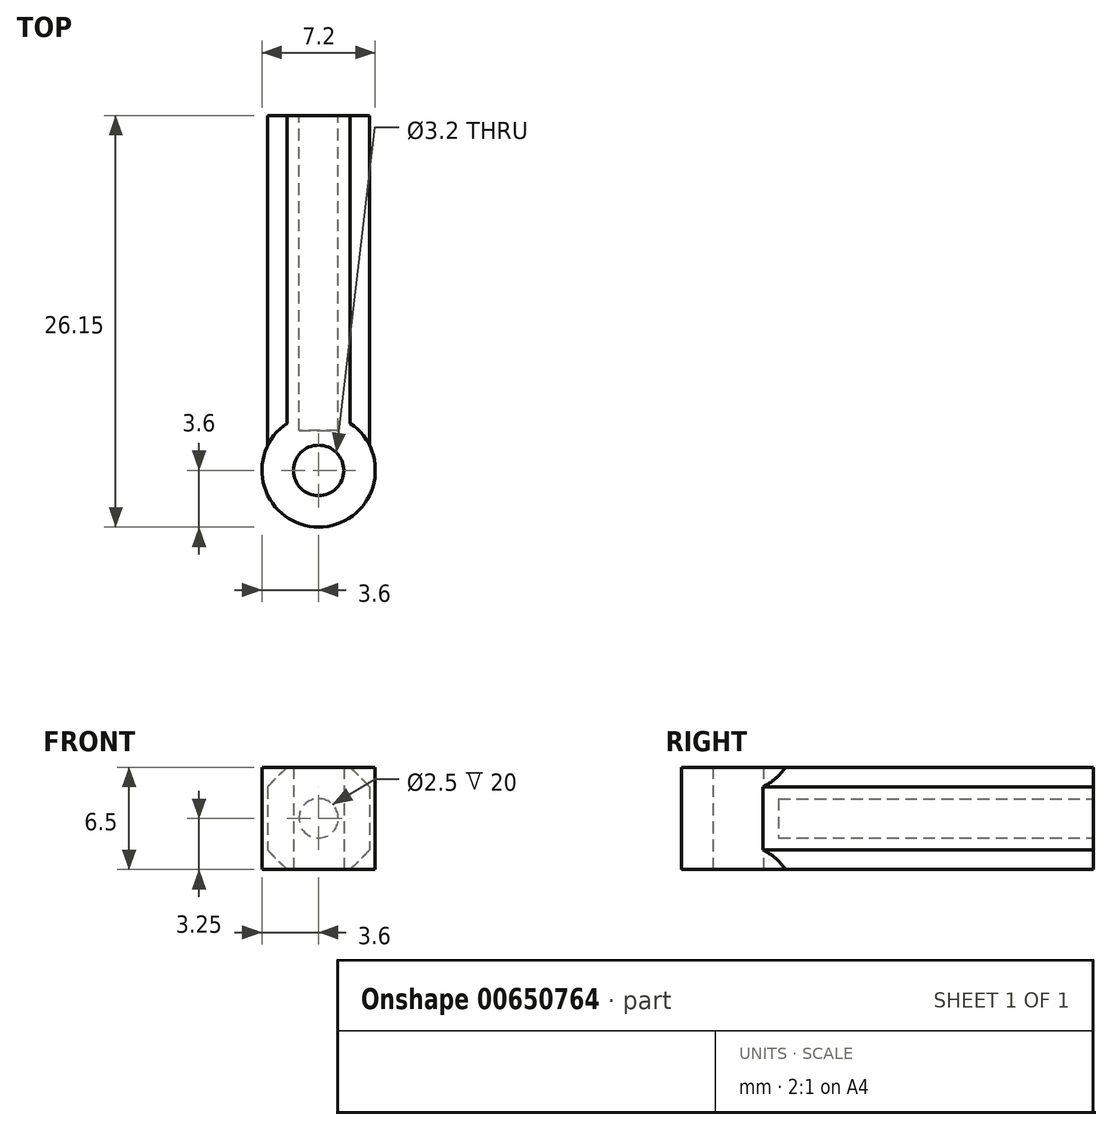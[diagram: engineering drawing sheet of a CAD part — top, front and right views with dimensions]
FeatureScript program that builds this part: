
annotation { "Feature Type Name" : "Feature", "Feature Type Description" : "" }
export const myFeature = defineFeature(function(context is Context, id is Id, definition is map)
    precondition{}
    {
        {
            assignVariable(context, id + "F0", {"name" : "ThreadDiameter", "anyValue" : 2.5});
        }
        {
            assignVariable(context, id + "F1", {"name" : "ThreadLength", "anyValue" : 20});
        }
        {
            var Q0;
            Q0=qCreatedBy(makeId("Top.planeOp"),FACE);
            var sketch = newSketch(context, id + "F2", { "sketchPlane" : qUnion([Q0])});
            skCircle(sketch, "E0", {"center": v(0, 0) * mm, "radius": 1.6 * mm});
            skCircle(sketch, "E1", {"center": v(0, 0) * mm, "radius": 3.6 * mm});
            skLineSegment(sketch, "E2.bottom", {"start": v(-3.25, 1.55) * mm, "end": v(3.25, 1.55) * mm});
            skLineSegment(sketch, "E2.top", {"start": v(-3.25, 22.55) * mm, "end": v(3.25, 22.55) * mm});
            skLineSegment(sketch, "E2.left", {"start": v(-3.25, 1.55) * mm, "end": v(-3.25, 22.55) * mm});
            skLineSegment(sketch, "E2.right", {"start": v(3.25, 1.55) * mm, "end": v(3.25, 22.55) * mm});
            skSolve(sketch);
        }
        {
            var Q0;
            Q0=makeQuery(id+"F2.imprint","IMPRINT",FACE,{"disambiguationData":[TD([[makeQuery(id+"F2.imprint","IMPRINT",EDGE,{"derivedFrom":sQuery(id+"F2.wireOp",EDGE,"E2.top")}),-1.0]])]});
            var Q1;
            {var subQ0=sQuery(id+"F2.wireOp",EDGE,"E2.bottom");var subQ1=sQuery(id+"F2.wireOp",EDGE,"E0");var subQ2=makeQuery(id+"F2.imprint","INTERSECT",VERTEX,{"disambiguationData":[OD(0.0)],"derivedFrom":[subQ1,subQ0]});Q1=makeQuery(id+"F2.imprint","IMPRINT",FACE,{"disambiguationData":[TD([[makeQuery(id+"F2.imprint","IMPRINT",EDGE,{"disambiguationData":[TD([[subQ2,-1.0]])],"derivedFrom":subQ1}),-1.0]])]});}
            var Q2;
            {var subQ0=sQuery(id+"F2.wireOp",EDGE,"E2.bottom");var subQ1=sQuery(id+"F2.wireOp",EDGE,"E0");var subQ2=makeQuery(id+"F2.imprint","INTERSECT",VERTEX,{"disambiguationData":[OD(0.0)],"derivedFrom":[subQ1,subQ0]});Q2=makeQuery(id+"F2.imprint","IMPRINT",FACE,{"disambiguationData":[TD([[makeQuery(id+"F2.imprint","IMPRINT",EDGE,{"disambiguationData":[TD([[subQ2,1.0]])],"derivedFrom":subQ1}),-1.0]])]});}
            extrude(context, id + "F3", {"entities" : qUnion([Q0, Q1, Q2]), "depth" : (getVariable(context, 'ThreadDiameter') + 4) * mm, "offsetDistance" : 25 * mm});
        }
        {
            var Q0;
            Q0=makeQuery(id+"F3.opExtrude","CAP_EDGE",EDGE,{"disambiguationData":[OSD([sQuery(id+"F2.wireOp",EDGE,"E2.right")])],"isStart":false});
            var Q1;
            Q1=makeQuery(id+"F3.opExtrude","CAP_EDGE",EDGE,{"disambiguationData":[OSD([sQuery(id+"F2.wireOp",EDGE,"E2.left")])],"isStart":false});
            var Q2;
            Q2=makeQuery(id+"F3.opExtrude","CAP_EDGE",EDGE,{"disambiguationData":[OSD([sQuery(id+"F2.wireOp",EDGE,"E2.right")])],"isStart":true});
            var Q3;
            Q3=makeQuery(id+"F3.opExtrude","CAP_EDGE",EDGE,{"disambiguationData":[OSD([sQuery(id+"F2.wireOp",EDGE,"E2.left")])],"isStart":true});
            chamfer(context, id + "F4", {"entities" : qUnion([Q0, Q1, Q2, Q3]), "width" : (getVariable(context, 'ThreadDiameter') / 2) * mm, "tangentPropagation" : true});
        }
        {
            var Q0;
            Q0=makeQuery(id+"F3.opExtrude","SWEPT_FACE",FACE,{"disambiguationData":[OSD([sQuery(id+"F2.wireOp",EDGE,"E2.top")])]});
            var sketch = newSketch(context, id + "F5", { "sketchPlane" : qUnion([Q0])});
            skCircle(sketch, "E3", {"center": v(0, 3.25) * mm, "radius": 1.25 * mm});
            skSolve(sketch);
        }
        {
            var Q0;
            Q0=makeQuery(id+"F5.imprint","IMPRINT",FACE,{"disambiguationData":[TD([[makeQuery(id+"F5.imprint","IMPRINT",EDGE,{"derivedFrom":sQuery(id+"F5.wireOp",EDGE,"E3")}),1.0]])]});
            extrude(context, id + "F6", {"entities" : qUnion([Q0]), "operationType" : NewBodyOperationType.REMOVE, "oppositeDirection" : true, "depth" : (getVariable(context, 'ThreadLength')) * mm, "offsetDistance" : 25 * mm});
        }
    });
